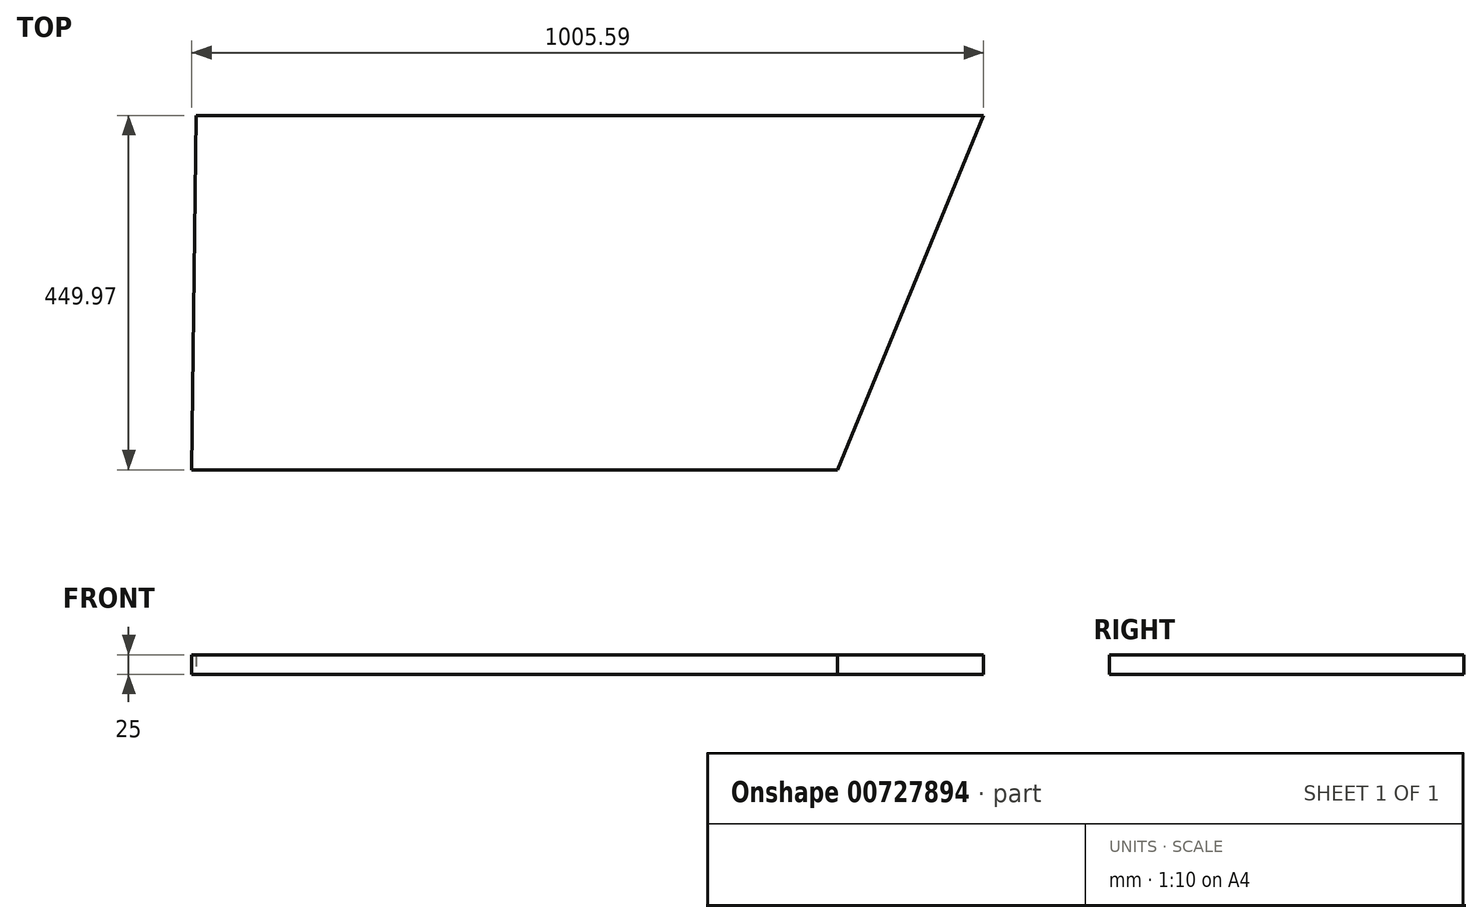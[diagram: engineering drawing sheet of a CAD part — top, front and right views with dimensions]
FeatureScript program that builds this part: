
annotation { "Feature Type Name" : "Feature", "Feature Type Description" : "" }
export const myFeature = defineFeature(function(context is Context, id is Id, definition is map)
    precondition{}
    {
        {
            var Q0;
            Q0=qCreatedBy(makeId("Top.planeOp"),FACE);
            var sketch = newSketch(context, id + "F0", { "sketchPlane" : qUnion([Q0])});
            skLineSegment(sketch, "E0", {"start": v(-814.41, 449.97) * mm, "end": v(185.59, 449.97) * mm});
            skLineSegment(sketch, "E1", {"start": v(185.59, 449.97) * mm, "end": v(0, 0) * mm});
            skLineSegment(sketch, "E2", {"start": v(0, 0) * mm, "end": v(-820, 0) * mm});
            skLineSegment(sketch, "E3", {"start": v(-820, 0) * mm, "end": v(-814.41, 449.97) * mm});
            skLineSegment(sketch, "E4", {"start": v(-815.47, 364.8) * mm, "end": v(150.46, 364.8) * mm});
            skLineSegment(sketch, "E5", {"start": v(-816.66, 269.13) * mm, "end": v(111, 269.13) * mm});
            skLineSegment(sketch, "E6", {"start": v(-817.74, 181.95) * mm, "end": v(75.05, 181.95) * mm});
            skLineSegment(sketch, "E7", {"start": v(-890.05, 0) * mm, "end": v(-890.05, 90) * mm});
            skLineSegment(sketch, "E8", {"start": v(-890.05, 90) * mm, "end": v(-890.05, 180) * mm});
            skLineSegment(sketch, "E9", {"start": v(-890.05, 180) * mm, "end": v(-890.05, 270) * mm});
            skLineSegment(sketch, "E10", {"start": v(-890.05, 270) * mm, "end": v(-890.05, 360) * mm});
            skLineSegment(sketch, "E11", {"start": v(-890.05, 360) * mm, "end": v(-890.05, 450) * mm});
            skLineSegment(sketch, "E12", {"start": v(-818.84, 93.13) * mm, "end": v(38.41, 93.13) * mm});
            skSolve(sketch);
        }
        {
            var Q0;
            Q0=qCreatedBy(makeId("Top.planeOp"),FACE);
            var sketch = newSketch(context, id + "F1", { "sketchPlane" : qUnion([Q0])});
            skSolve(sketch);
        }
        {
            var Q0;
            Q0 = qSketchRegion(id + "F1", true);
            var Q1;
            {var subQ0=sQuery(id+"F0.wireOp",EDGE,"E0");Q1=makeQuery(id+"F0.imprint","IMPRINT",FACE,{"disambiguationData":[TD([[makeQuery(id+"F0.imprint","IMPRINT",EDGE,{"derivedFrom":subQ0}),-1.0]])]});}
            var Q2;
            {var subQ0=sQuery(id+"F0.wireOp",EDGE,"E4");Q2=makeQuery(id+"F0.imprint","IMPRINT",FACE,{"disambiguationData":[TD([[makeQuery(id+"F0.imprint","IMPRINT",EDGE,{"derivedFrom":subQ0}),-1.0]])]});}
            var Q3;
            {var subQ0=sQuery(id+"F0.wireOp",EDGE,"E6");Q3=makeQuery(id+"F0.imprint","IMPRINT",FACE,{"disambiguationData":[TD([[makeQuery(id+"F0.imprint","IMPRINT",EDGE,{"derivedFrom":subQ0}),-1.0]])]});}
            var Q4;
            {var subQ0=sQuery(id+"F0.wireOp",EDGE,"E5");Q4=makeQuery(id+"F0.imprint","IMPRINT",FACE,{"disambiguationData":[TD([[makeQuery(id+"F0.imprint","IMPRINT",EDGE,{"derivedFrom":subQ0}),-1.0]])]});}
            var Q5;
            {var subQ0=sQuery(id+"F0.wireOp",EDGE,"E2");Q5=makeQuery(id+"F0.imprint","IMPRINT",FACE,{"disambiguationData":[TD([[makeQuery(id+"F0.imprint","IMPRINT",EDGE,{"derivedFrom":subQ0}),-1.0]])]});}
            extrude(context, id + "F2", {"entities" : qUnion([Q0, Q1, Q2, Q3, Q4, Q5]), "endBound" : BoundingType.SYMMETRIC, "depth" : 25 * mm, "offsetDistance" : 25 * mm});
        }
    });
